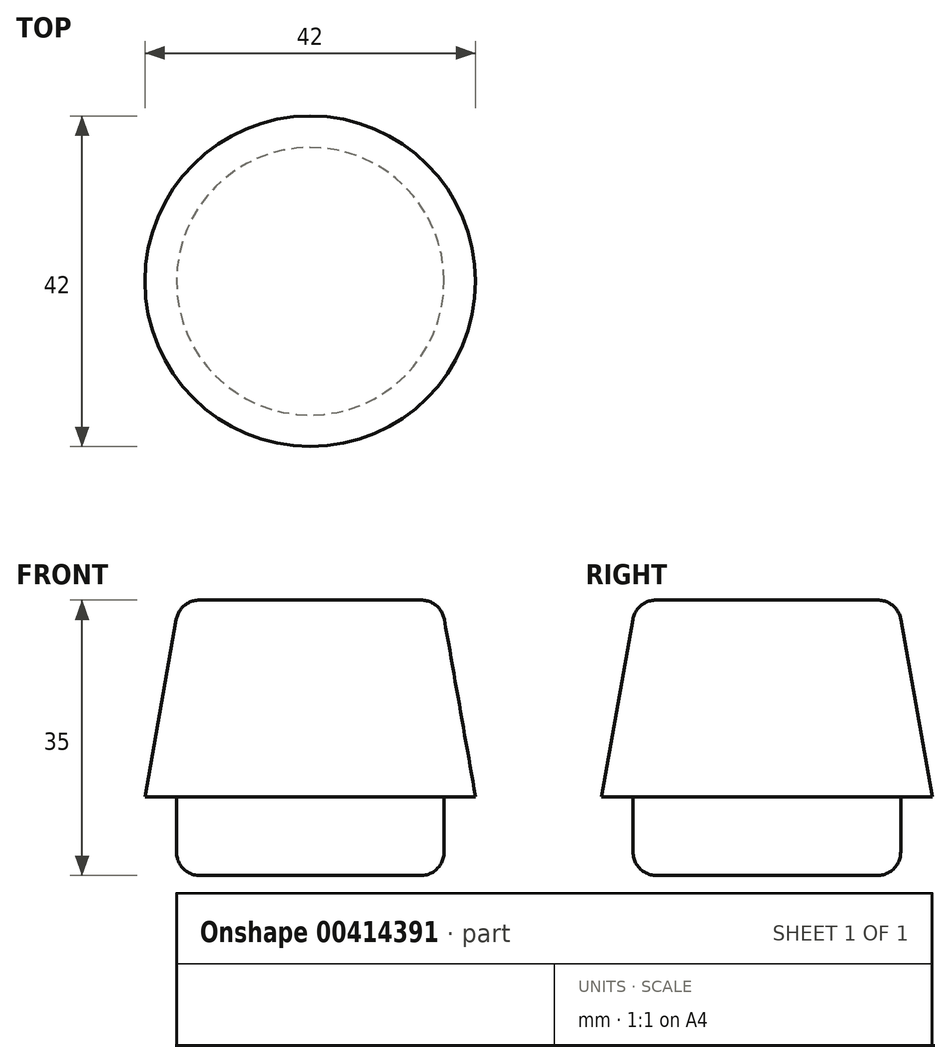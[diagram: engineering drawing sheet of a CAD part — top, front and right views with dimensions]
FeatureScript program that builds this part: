
annotation { "Feature Type Name" : "Feature", "Feature Type Description" : "" }
export const myFeature = defineFeature(function(context is Context, id is Id, definition is map)
    precondition{}
    {
        {
            var Q0;
            Q0=qCreatedBy(makeId("Top.planeOp"),FACE);
            var sketch = newSketch(context, id + "F0", { "sketchPlane" : qUnion([Q0])});
            skCircle(sketch, "E0", {"center": v(0, 0) * mm, "radius": 17 * mm});
            skSolve(sketch);
        }
        {
            var Q0;
            Q0 = qSketchRegion(id + "F0", true);
            extrude(context, id + "F1", {"entities" : qUnion([Q0]), "depth" : 10 * mm});
        }
        {
            var Q0;
            Q0=makeQuery(id+"F1.opExtrude","CAP_FACE",FACE,{"disambiguationData":[OSD([sQuery(id+"F0.wireOp",EDGE,"E0")])],"isStart":false});
            var sketch = newSketch(context, id + "F2", { "sketchPlane" : qUnion([Q0])});
            skCircle(sketch, "E1", {"center": v(0, 0) * mm, "radius": 21 * mm});
            skSolve(sketch);
        }
        {
            var Q0;
            Q0 = qSketchRegion(id + "F2", true);
            extrude(context, id + "F3", {"entities" : qUnion([Q0]), "operationType" : NewBodyOperationType.ADD, "depth" : 25 * mm, "hasDraft" : true, "draftAngle" : 10 * degree, "draftPullDirection" : true});
        }
        {
            var Q0;
            Q0=makeQuery(id+"F3.opExtrude","CAP_EDGE",EDGE,{"disambiguationData":[OSD([sQuery(id+"F2.wireOp",EDGE,"E1")])],"isStart":false});
            var Q1;
            Q1=makeQuery(id+"F1.opExtrude","CAP_EDGE",EDGE,{"disambiguationData":[OSD([sQuery(id+"F0.wireOp",EDGE,"E0")])],"isStart":true});
            fillet(context, id + "F4", {"entities" : qUnion([Q0, Q1]), "radius" : 3 * mm, "tangentPropagation" : true, "allowEdgeOverflow" : false});
        }
    });
